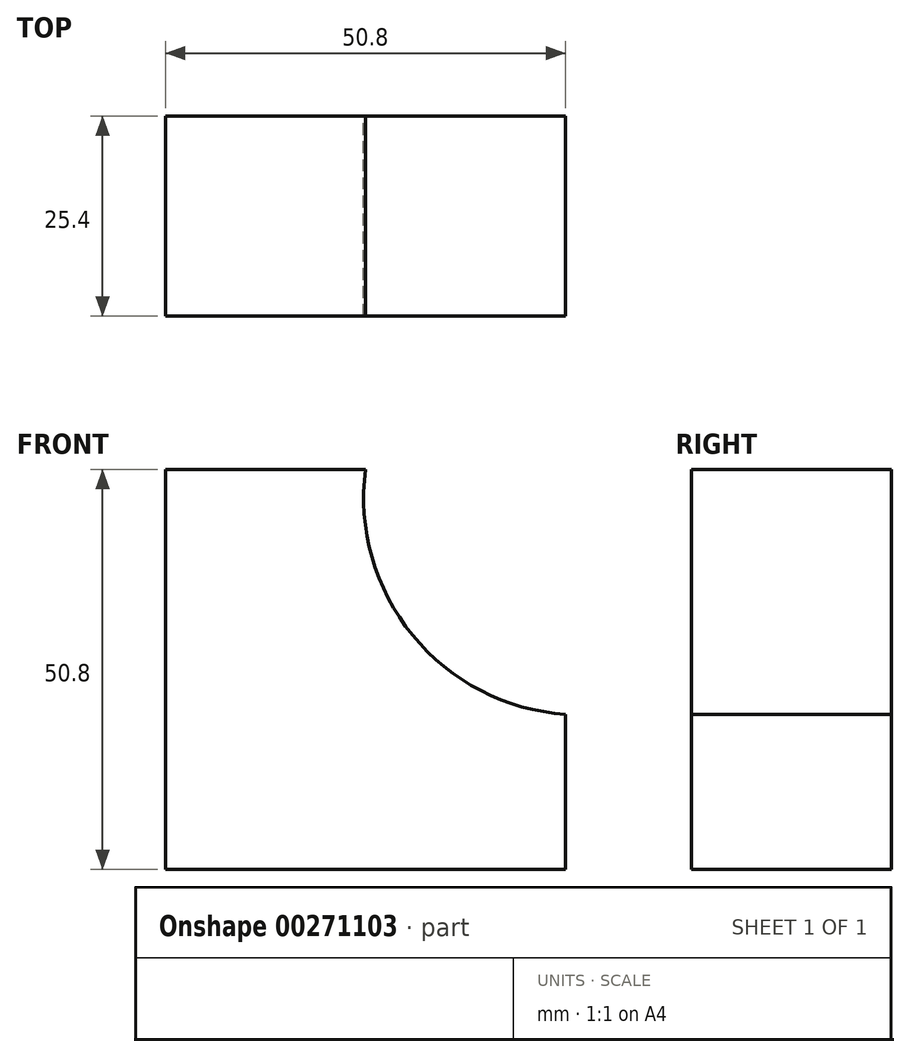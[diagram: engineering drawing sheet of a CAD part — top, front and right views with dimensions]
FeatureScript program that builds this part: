
annotation { "Feature Type Name" : "Feature", "Feature Type Description" : "" }
export const myFeature = defineFeature(function(context is Context, id is Id, definition is map)
    precondition{}
    {
        {
            var Q0;
            Q0=qCreatedBy(makeId("Front.planeOp"),FACE);
            var sketch = newSketch(context, id + "F0", { "sketchPlane" : qUnion([Q0])});
            skLineSegment(sketch, "E0", {"start": v(0, 0) * mm, "end": v(-50.8, 0) * mm});
            skLineSegment(sketch, "E1", {"start": v(-50.8, 50.8) * mm, "end": v(-50.8, 0) * mm});
            skLineSegment(sketch, "E2", {"start": v(-50.8, 50.8) * mm, "end": v(-25.4, 50.8) * mm});
            skLineSegment(sketch, "E3", {"start": v(0, 0) * mm, "end": v(0, 19.7) * mm});
            skArc(sketch, "E4", {"start": v(-25.4, 50.8) * mm, "mid": v(-19.42, 29.76) * mm, "end": v(0, 19.7) * mm});
            skSolve(sketch);
        }
        {
            var Q0;
            Q0 = qSketchRegion(id + "F0", true);
            extrude(context, id + "F1", {"entities" : qUnion([Q0]), "depth" : 25.4 * mm});
        }
    });
